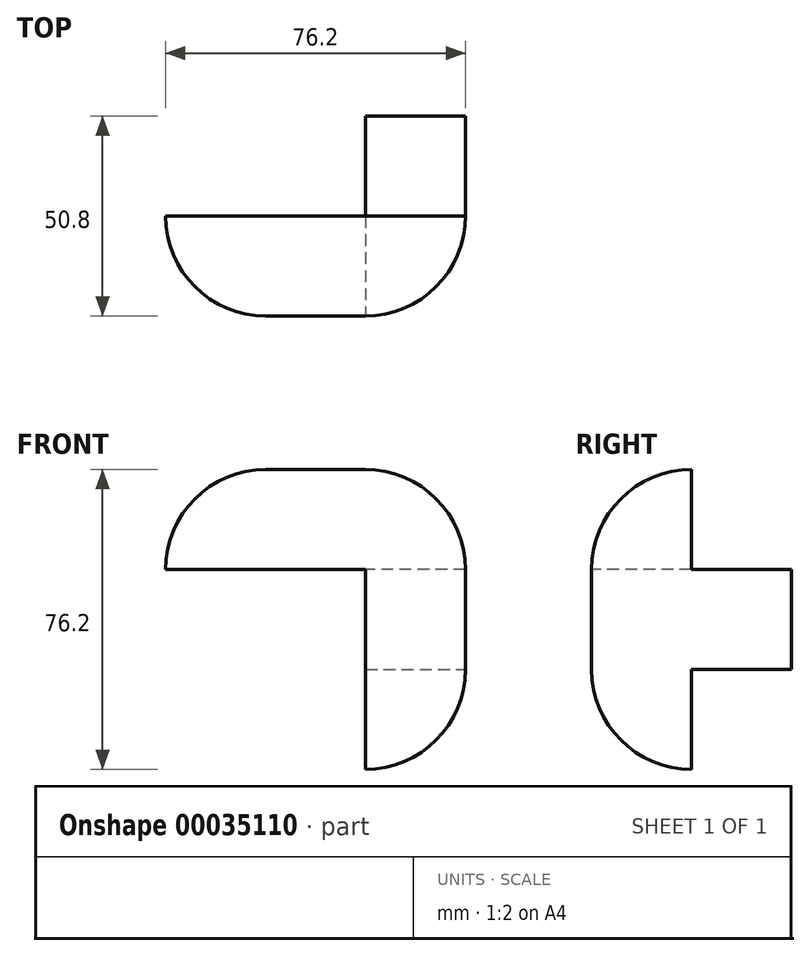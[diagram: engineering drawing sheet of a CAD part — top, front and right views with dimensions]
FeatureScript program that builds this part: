
annotation { "Feature Type Name" : "Feature", "Feature Type Description" : "" }
export const myFeature = defineFeature(function(context is Context, id is Id, definition is map)
    precondition{}
    {
        {
            var Q0;
            Q0=qCreatedBy(makeId("Top.planeOp"),FACE);
            var sketch = newSketch(context, id + "F0", { "sketchPlane" : qUnion([Q0])});
            skLineSegment(sketch, "E0", {"start": v(0, 0) * mm, "end": v(0, 25.4) * mm});
            skLineSegment(sketch, "E1", {"start": v(0, 25.4) * mm, "end": v(25.4, 25.4) * mm});
            skLineSegment(sketch, "E2", {"start": v(25.4, 25.4) * mm, "end": v(25.4, 0) * mm});
            skLineSegment(sketch, "E3", {"start": v(25.4, 0) * mm, "end": v(0, 0) * mm});
            skSolve(sketch);
        }
        {
            var Q0;
            Q0=makeQuery(id+"F0.imprint","IMPRINT",FACE,{"disambiguationData":[TD([[makeQuery(id+"F0.imprint","IMPRINT",EDGE,{"derivedFrom":sQuery(id+"F0.wireOp",EDGE,"E0")}),-1.0]])]});
            extrude(context, id + "F1", {"entities" : qUnion([Q0]), "depth" : 76.2 * mm});
        }
        {
            var Q0;
            Q0=makeQuery(id+"F1.opExtrude","SWEPT_FACE",FACE,{"disambiguationData":[OSD([sQuery(id+"F0.wireOp",EDGE,"E0")])]});
            var sketch = newSketch(context, id + "F2", { "sketchPlane" : qUnion([Q0])});
            skLineSegment(sketch, "E4", {"start": v(-25.4, 76.2) * mm, "end": v(-25.4, 50.8) * mm});
            skLineSegment(sketch, "E5", {"start": v(-25.4, 50.8) * mm, "end": v(0, 50.8) * mm});
            skLineSegment(sketch, "E6", {"start": v(0, 50.8) * mm, "end": v(0, 76.2) * mm});
            skLineSegment(sketch, "E7", {"start": v(0, 76.2) * mm, "end": v(-25.4, 76.2) * mm});
            skSolve(sketch);
        }
        {
            var Q0;
            Q0=makeQuery(id+"F2.imprint","IMPRINT",FACE,{"disambiguationData":[TD([[makeQuery(id+"F2.imprint","IMPRINT",EDGE,{"derivedFrom":sQuery(id+"F2.wireOp",EDGE,"E4")}),1.0]])]});
            extrude(context, id + "F3", {"entities" : qUnion([Q0]), "operationType" : NewBodyOperationType.ADD, "depth" : 50.8 * mm});
        }
        {
            var Q0;
            Q0=makeQuery(id+"F3.boolean.opBoolean","MERGE",FACE,{"derivedFrom":[makeQuery(id+"F1.opExtrude","SWEPT_FACE",FACE,{"disambiguationData":[OSD([sQuery(id+"F0.wireOp",EDGE,"E1")])]}),makeQuery(id+"F3.opExtrude","SWEPT_FACE",FACE,{"disambiguationData":[OSD([sQuery(id+"F2.wireOp",EDGE,"E4")])]})]});
            var sketch = newSketch(context, id + "F4", { "sketchPlane" : qUnion([Q0])});
            skLineSegment(sketch, "E8", {"start": v(0, 50.8) * mm, "end": v(0, 25.4) * mm});
            skLineSegment(sketch, "E9", {"start": v(0, 25.4) * mm, "end": v(-25.4, 25.4) * mm});
            skLineSegment(sketch, "E10", {"start": v(-25.4, 25.4) * mm, "end": v(-25.4, 50.8) * mm});
            skLineSegment(sketch, "E11", {"start": v(-25.4, 50.8) * mm, "end": v(0, 50.8) * mm});
            skSolve(sketch);
        }
        {
            var Q0;
            Q0=makeQuery(id+"F4.imprint","IMPRINT",FACE,{"disambiguationData":[TD([[makeQuery(id+"F4.imprint","IMPRINT",EDGE,{"derivedFrom":sQuery(id+"F4.wireOp",EDGE,"E8")}),-1.0]])]});
            extrude(context, id + "F5", {"entities" : qUnion([Q0]), "operationType" : NewBodyOperationType.ADD, "depth" : 25.4 * mm});
        }
        {
            var Q0;
            Q0=makeQuery(id+"F3.opExtrude","CAP_EDGE",EDGE,{"disambiguationData":[OSD([sQuery(id+"F2.wireOp",EDGE,"E7")])],"isStart":false});
            var Q1;
            Q1=makeQuery(id+"F3.opExtrude","CAP_EDGE",EDGE,{"disambiguationData":[OSD([sQuery(id+"F2.wireOp",EDGE,"E6")])],"isStart":false});
            var Q2;
            Q2=makeQuery(id+"F3.boolean.opBoolean","MERGE",EDGE,{"derivedFrom":[makeQuery(id+"F1.opExtrude","CAP_EDGE",EDGE,{"disambiguationData":[OSD([sQuery(id+"F0.wireOp",EDGE,"E3")])],"isStart":false}),makeQuery(id+"F3.opExtrude","SWEPT_EDGE",EDGE,{"disambiguationData":[OSD([sQuery(id+"F2.wireOp",EDGE,"E6"),sQuery(id+"F2.wireOp",EDGE,"E7")])]})]});
            var Q3;
            Q3=makeQuery(id+"F1.opExtrude","SWEPT_EDGE",EDGE,{"disambiguationData":[OSD([sQuery(id+"F0.wireOp",EDGE,"E2"),sQuery(id+"F0.wireOp",EDGE,"E3")])]});
            var Q4;
            Q4=makeQuery(id+"F1.opExtrude","CAP_EDGE",EDGE,{"disambiguationData":[OSD([sQuery(id+"F0.wireOp",EDGE,"E2")])],"isStart":true});
            var Q5;
            Q5=makeQuery(id+"F1.opExtrude","CAP_EDGE",EDGE,{"disambiguationData":[OSD([sQuery(id+"F0.wireOp",EDGE,"E3")])],"isStart":true});
            var Q6;
            Q6=makeQuery(id+"F1.opExtrude","CAP_EDGE",EDGE,{"disambiguationData":[OSD([sQuery(id+"F0.wireOp",EDGE,"E2")])],"isStart":false});
            fillet(context, id + "F6", {"entities" : qUnion([Q0, Q1, Q2, Q3, Q4, Q5, Q6]), "radius" : 25.4 * mm, "tangentPropagation" : true, "allowEdgeOverflow" : false});
        }
    });
